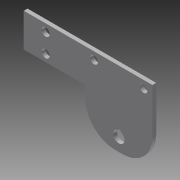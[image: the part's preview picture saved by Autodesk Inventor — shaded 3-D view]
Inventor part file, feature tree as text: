
AUTODESK INVENTOR PART (.ipt)
format: ipt  version: 2013 (Build 170138000, 138)  size: 162,816 bytes
history: native  units: in
note: dims shown in document units (in); Inventor stores cm internally (conversion verified against a paired STEP export)
features: sketch x5, other x5, reference x4, sheet_metal_op x1, extrude x1, fillet x1
ambient origin geometry x8: Origin, YZ Plane, XZ Plane, XY Plane, X Axis, Y Axis, Z Axis, Center Point
feature tree (17):
  sheet_metal_op  "Face3"
  extrude  "Extrusion2"  Depth=0.25in
  sketch  "Sketch8"  dims[d8=0.125in]
  fillet  "Fillet1"  Radius=0.295in
  sketch  "Sketch11"  dims[d60=2.5in d61=0.4375in d62=0.375in d63=0.125in d67=0.125in d68=0.0in d69=2.053in d70=0.0in d71=1.125in d72=2.053in d75=0.125in d76=0.0in d77=0.125in d78=0.0in d79=0.125in d80=0.0in d81=1.0in d82=0.0469in d86=0.0938in d87=0.0469in]
  other  "Plate6"
  sketch  "Sketch7"  dims[d3=0.295in d4=0.25in d5=0.295in]
  reference  "Reference1"
  reference  "Reference2"
  sketch  "Sketch9"  dims[d19=0.25in]
  sketch  "Sketch10"  dims[d56=0.125in]
  reference  "Reference3"
  reference  "Reference4"
  other  "Cut1"
  other  "Cut3"
  other  "Cut4"
  other  "Cut5"
